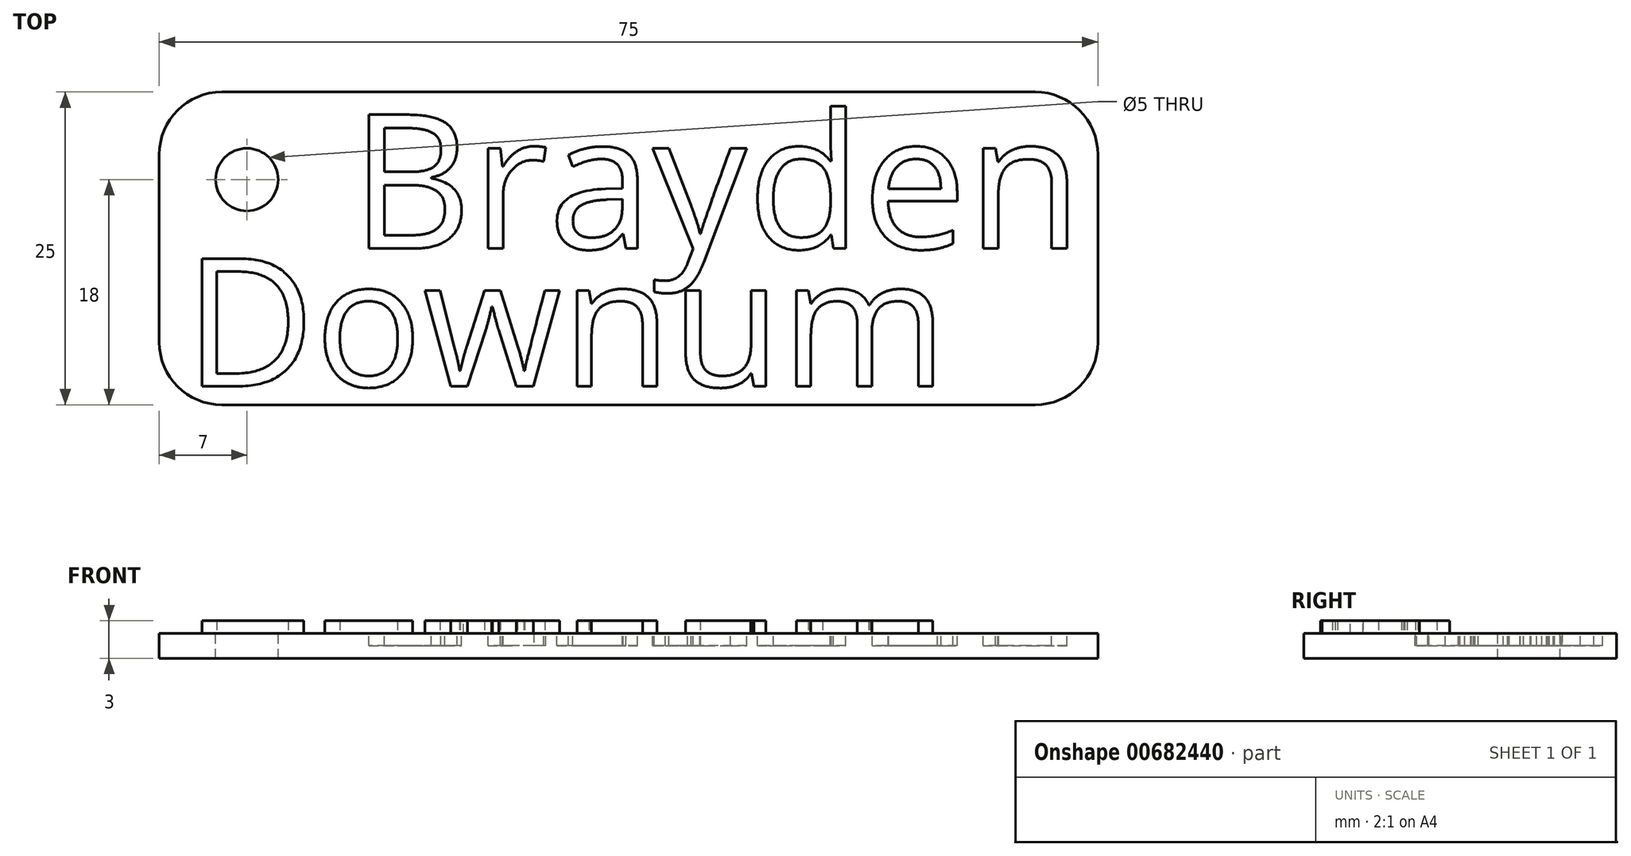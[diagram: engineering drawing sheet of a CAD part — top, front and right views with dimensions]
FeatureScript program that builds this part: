
annotation { "Feature Type Name" : "Feature", "Feature Type Description" : "" }
export const myFeature = defineFeature(function(context is Context, id is Id, definition is map)
    precondition{}
    {
        {
            var Q0;
            Q0=qCreatedBy(makeId("Top.planeOp"),FACE);
            var sketch = newSketch(context, id + "F0", { "sketchPlane" : qUnion([Q0])});
            skLineSegment(sketch, "E0.bottom", {"start": v(32.5, 12.5) * mm, "end": v(-32.5, 12.5) * mm});
            skLineSegment(sketch, "E0.top", {"start": v(32.5, -12.5) * mm, "end": v(-32.5, -12.5) * mm});
            skLineSegment(sketch, "E0.left", {"start": v(37.5, 7.5) * mm, "end": v(37.5, -7.5) * mm});
            skLineSegment(sketch, "E0.right", {"start": v(-37.5, 7.5) * mm, "end": v(-37.5, -7.5) * mm});
            skPoint(sketch, "E0.middle", {"position": v(0, 0) * mm});
            skPoint(sketch, "E1.visualSharp", {"position": v(-37.5, 12.5) * mm});
            skArc(sketch, "E1.filletArc", {"start": v(-32.5, 12.5) * mm, "mid": v(-36.04, 11.04) * mm, "end": v(-37.5, 7.5) * mm});
            skPoint(sketch, "E2.visualSharp", {"position": v(37.5, 12.5) * mm});
            skArc(sketch, "E2.filletArc", {"start": v(37.5, 7.5) * mm, "mid": v(36.04, 11.04) * mm, "end": v(32.5, 12.5) * mm});
            skPoint(sketch, "E3.visualSharp", {"position": v(37.5, -12.5) * mm});
            skArc(sketch, "E3.filletArc", {"start": v(32.5, -12.5) * mm, "mid": v(36.04, -11.04) * mm, "end": v(37.5, -7.5) * mm});
            skPoint(sketch, "E4.visualSharp", {"position": v(-37.5, -12.5) * mm});
            skArc(sketch, "E4.filletArc", {"start": v(-37.5, -7.5) * mm, "mid": v(-36.04, -11.04) * mm, "end": v(-32.5, -12.5) * mm});
            skSolve(sketch);
        }
        {
            var Q0;
            Q0=makeQuery(id+"F0.imprint","IMPRINT",FACE,{"disambiguationData":[TD([[makeQuery(id+"F0.imprint","IMPRINT",EDGE,{"derivedFrom":sQuery(id+"F0.wireOp",EDGE,"E0.bottom")}),1.0]])]});
            extrude(context, id + "F1", {"entities" : qUnion([Q0]), "depth" : 2 * mm, "offsetDistance" : 25 * mm});
        }
        {
            var Q0;
            Q0=makeQuery(id+"F1.opExtrude","CAP_FACE",FACE,{"disambiguationData":[OSD([sQuery(id+"F0.wireOp",EDGE,"E0.bottom"),sQuery(id+"F0.wireOp",EDGE,"E0.top"),sQuery(id+"F0.wireOp",EDGE,"E0.left"),sQuery(id+"F0.wireOp",EDGE,"E0.right"),sQuery(id+"F0.wireOp",EDGE,"E1.filletArc"),sQuery(id+"F0.wireOp",EDGE,"E2.filletArc"),sQuery(id+"F0.wireOp",EDGE,"E3.filletArc"),sQuery(id+"F0.wireOp",EDGE,"E4.filletArc")])],"isStart":false});
            var sketch = newSketch(context, id + "F2", { "sketchPlane" : qUnion([Q0])});
            skPoint(sketch, "E5", {"position": v(-30.5, 5.5) * mm});
            skSolve(sketch);
        }
        {
            var Q0;
            Q0=sQuery(id+"F2.wireOp",VERTEX,"E5");
            var Q1;
            Q1=makeQuery(id+"F1.opExtrude","SWEPT_BODY",BODY,{"disambiguationData":[OSD([sQuery(id+"F0.wireOp",EDGE,"E0.bottom"),sQuery(id+"F0.wireOp",EDGE,"E0.top"),sQuery(id+"F0.wireOp",EDGE,"E0.left"),sQuery(id+"F0.wireOp",EDGE,"E0.right"),sQuery(id+"F0.wireOp",EDGE,"E1.filletArc"),sQuery(id+"F0.wireOp",EDGE,"E2.filletArc"),sQuery(id+"F0.wireOp",EDGE,"E3.filletArc"),sQuery(id+"F0.wireOp",EDGE,"E4.filletArc")])]});
            hole(context, id + "F3", {"style" : HoleStyle.SIMPLE, "endStyle" : HoleEndStyle.THROUGH, "holeDiameter" : 5 * mm, "majorDiameter" : 5 * mm, "isTappedThrough" : true, "tappedDepth" : 12 * mm, "tapClearance" : 3, "locations" : qUnion([Q0]), "scope" : qUnion([Q1])});
        }
        {
            var Q0;
            Q0=makeQuery(id+"F1.opExtrude","CAP_FACE",FACE,{"disambiguationData":[OSD([sQuery(id+"F0.wireOp",EDGE,"E0.bottom"),sQuery(id+"F0.wireOp",EDGE,"E0.top"),sQuery(id+"F0.wireOp",EDGE,"E0.left"),sQuery(id+"F0.wireOp",EDGE,"E0.right"),sQuery(id+"F0.wireOp",EDGE,"E1.filletArc"),sQuery(id+"F0.wireOp",EDGE,"E2.filletArc"),sQuery(id+"F0.wireOp",EDGE,"E3.filletArc"),sQuery(id+"F0.wireOp",EDGE,"E4.filletArc")])],"isStart":false});
            var sketch = newSketch(context, id + "F4", { "sketchPlane" : qUnion([Q0])});
            skText(sketch, "E6", { "text": "Brayden ", "fontName": "OpenSans-Regular.ttf"});
            const initialGuessF4  = {"E6": [-0.02222, 0, 1, 0, 0.01078]};
            skSetInitialGuess(sketch, initialGuessF4);
            skSolve(sketch);
        }
        {
            var Q0;
            Q0 = qSketchRegion(id + "F4", true);
            extrude(context, id + "F5", {"entities" : qUnion([Q0]), "operationType" : NewBodyOperationType.REMOVE, "oppositeDirection" : true, "depth" : 1 * mm, "offsetDistance" : 25 * mm});
        }
        {
            var Q0;
            {var subQ0=sQuery(id+"F0.wireOp",EDGE,"E4.filletArc");var subQ1=sQuery(id+"F0.wireOp",EDGE,"E1.filletArc");var subQ2=sQuery(id+"F0.wireOp",EDGE,"E0.bottom");var subQ3=sQuery(id+"F0.wireOp",EDGE,"E2.filletArc");var subQ4=sQuery(id+"F0.wireOp",EDGE,"E0.left");var subQ5=sQuery(id+"F0.wireOp",EDGE,"E0.top");var subQ6=sQuery(id+"F0.wireOp",EDGE,"E0.right");var subQ7=sQuery(id+"F0.wireOp",EDGE,"E3.filletArc");Q0=makeQuery(id+"F5.boolean.opBoolean","SPLIT",FACE,{"disambiguationData":[TD([makeQuery(id+"F1.opExtrude","SWEPT_FACE",FACE,{"disambiguationData":[OSD([subQ2])]})])],"derivedFrom":makeQuery(id+"F1.opExtrude","CAP_FACE",FACE,{"disambiguationData":[OSD([subQ2,subQ5,subQ4,subQ6,subQ1,subQ3,subQ7,subQ0])],"isStart":false})});}
            var sketch = newSketch(context, id + "F6", { "sketchPlane" : qUnion([Q0])});
            skText(sketch, "E7", { "text": "Downum \n", "fontName": "OpenSans-Regular.ttf"});
            const initialGuessF6  = {"E7": [-0.03548, -0.01102, 1, 0, 0.01028]};
            skSetInitialGuess(sketch, initialGuessF6);
            skSolve(sketch);
        }
        {
            var Q0;
            Q0 = qSketchRegion(id + "F6", true);
            extrude(context, id + "F7", {"entities" : qUnion([Q0]), "operationType" : NewBodyOperationType.ADD, "depth" : 1 * mm, "offsetDistance" : 25 * mm});
        }
    });
